# Revit family: ELDAR
name_source: partatom
category: Luminaires
units: mm (PartAtom-declared; Revit-internal decimal feet)

## family parameters
Cote de connecteur circulaire = Utiliser le diamètre
Couper avec des vides une fois chargée = Oui
Hôte = Face
Numéro OmniClass = 23.80.70.11.14.11
Partagée = Oui
Point de calcul de pièce = Oui
Source d'éclairage = Oui
Titre OmniClass = Downlights
Type d'élément = Normal

## types (4) — shared parameters
Angle de l'inclinaison = 60.00°
Diamètre intérieur = 101 mm  [stored 0.331365 ft]
Emettre la visibilité des formes dans le rendu = Non
Emettre à partir du diamètre du cercle = 610 mm
Fabricant = Résistex
Filtre de couleur = 16777215
Garantie = 5 ans
Gradation des changements de température de couleur de lampe = <Aucun>
IK = 06
IP = 54
Image du type = <Aucun>
Indice de charge = Eclairage
Matériau collerette = PC Transparent
Modèle = Eldar
Nombre pôles = 1
Rayon collerette = 73 mm
Rayon corps = 63 mm
Tension = 230 V
URL = https://www.resistex-sa.com
Épaisseur = 76 mm  [stored 0.249344 ft]
Épaisseur collerette = 2 mm  [stored 0.00656168 ft]
zero-valued in all types: Elévation par défaut

## per-type parameters (varying)
| type | Charge apparente | Commentaires relatifs à la puissance | Coût | Description | Fichier de distribution photométrique |
| 962600 | 24 VA | 23.5W | 72.5 $ | Downlight équipé d'une COB, efficacité lumineuse de 109lm/W | 962600.ies |
| 962601 | 26 VA | 25W | 72.5 $ | Downlight équipé d'une COB, efficacité lumineuse de 111lm/W | 962601.ies |
| 962603 | 24 VA | 23.5W | 105 $ | Downlight équipé d'une COB, efficacité lumineuse de 108.8lm/W | 962603.ies |
| 962602 | 26 VA | 25W | 105 $ | Downlight équipé d'une COB, efficacité lumineuse de 111lm/W | 962602.ies |

note: [stored X ft] marks values corroborated as IEEE doubles in the binary element streams (Revit-internal decimal feet)
